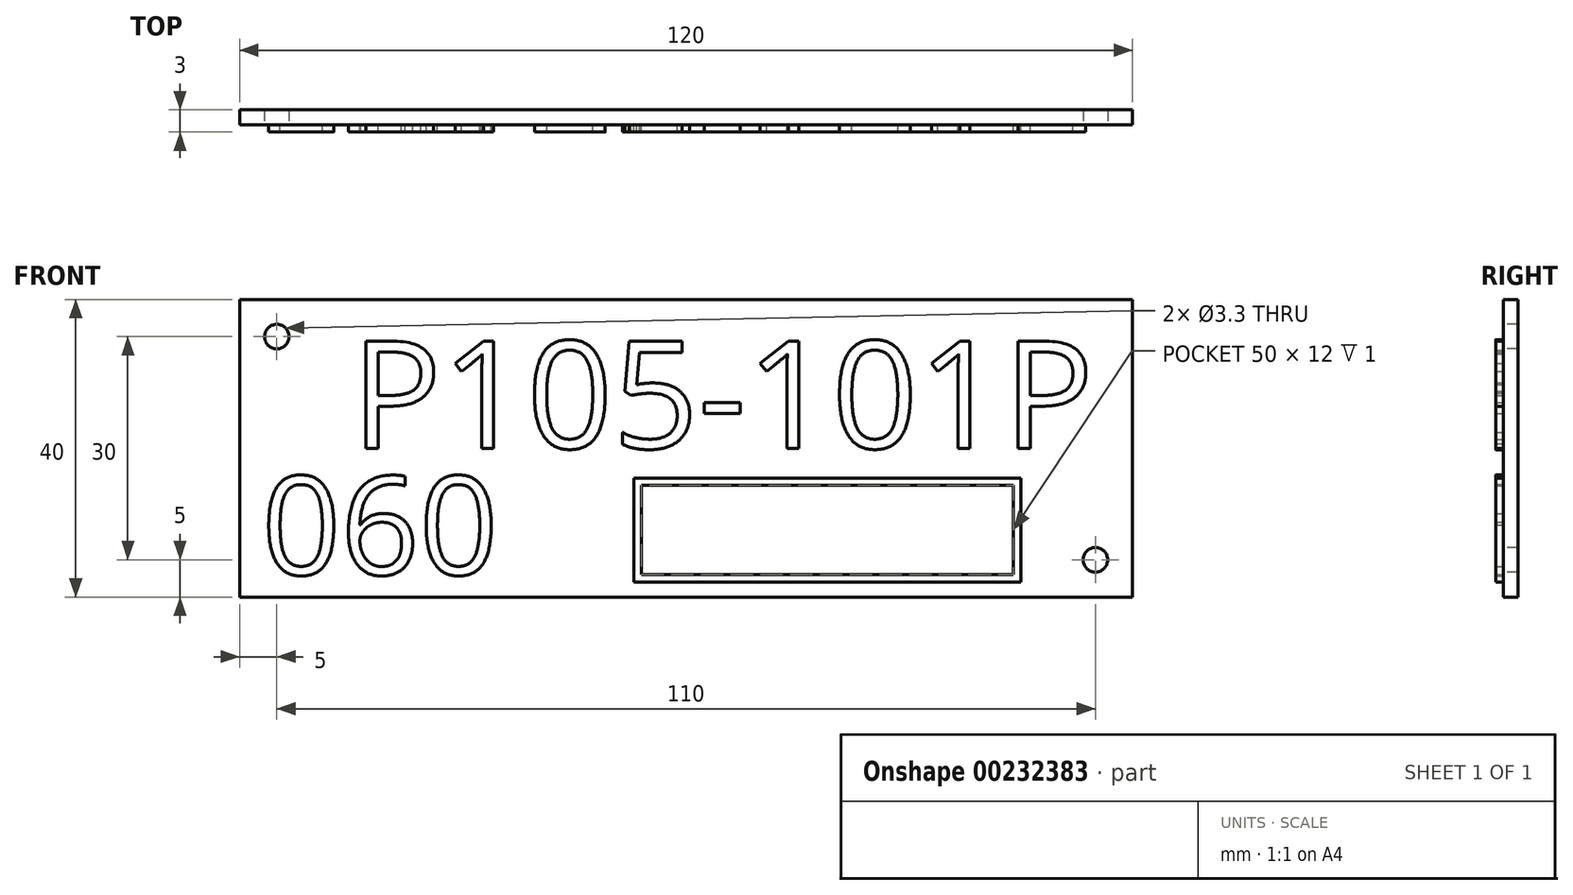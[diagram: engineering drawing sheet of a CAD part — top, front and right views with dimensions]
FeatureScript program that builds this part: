
annotation { "Feature Type Name" : "Feature", "Feature Type Description" : "" }
export const myFeature = defineFeature(function(context is Context, id is Id, definition is map)
    precondition{}
    {
        {
            var Q0;
            Q0=qCreatedBy(makeId("Front.planeOp"),FACE);
            var sketch = newSketch(context, id + "F0", { "sketchPlane" : qUnion([Q0])});
            skLineSegment(sketch, "E0.bottom", {"start": v(60, -20) * mm, "end": v(-60, -20) * mm});
            skLineSegment(sketch, "E0.top", {"start": v(60, 20) * mm, "end": v(-60, 20) * mm});
            skLineSegment(sketch, "E0.left", {"start": v(60, -20) * mm, "end": v(60, 20) * mm});
            skLineSegment(sketch, "E0.right", {"start": v(-60, -20) * mm, "end": v(-60, 20) * mm});
            skPoint(sketch, "E0.middle", {"position": v(0, 0) * mm});
            skSolve(sketch);
        }
        {
            var Q0;
            Q0=makeQuery(id+"F0.imprint","IMPRINT",FACE,{"disambiguationData":[TD([[makeQuery(id+"F0.imprint","IMPRINT",EDGE,{"derivedFrom":sQuery(id+"F0.wireOp",EDGE,"E0.bottom")}),-1.0]])]});
            extrude(context, id + "F1", {"entities" : qUnion([Q0]), "depth" : 2 * mm});
        }
        {
            var Q0;
            Q0=makeQuery(id+"F1.opExtrude","CAP_FACE",FACE,{"disambiguationData":[OSD([sQuery(id+"F0.wireOp",EDGE,"E0.bottom"),sQuery(id+"F0.wireOp",EDGE,"E0.top"),sQuery(id+"F0.wireOp",EDGE,"E0.left"),sQuery(id+"F0.wireOp",EDGE,"E0.right")])],"isStart":false});
            var sketch = newSketch(context, id + "F2", { "sketchPlane" : qUnion([Q0])});
            skPoint(sketch, "E1", {"position": v(-55, 15) * mm});
            skPoint(sketch, "E2", {"position": v(55, -15) * mm});
            skSolve(sketch);
        }
        {
            var Q0;
            Q0=sQuery(id+"F2.wireOp",VERTEX,"E1");
            var Q1;
            Q1=sQuery(id+"F2.wireOp",VERTEX,"E2");
            var Q2;
            Q2=makeQuery(id+"F1.opExtrude","SWEPT_BODY",BODY,{"disambiguationData":[OSD([sQuery(id+"F0.wireOp",EDGE,"E0.bottom"),sQuery(id+"F0.wireOp",EDGE,"E0.top"),sQuery(id+"F0.wireOp",EDGE,"E0.left"),sQuery(id+"F0.wireOp",EDGE,"E0.right")])]});
            hole(context, id + "F3", {"style" : HoleStyle.SIMPLE, "endStyle" : HoleEndStyle.THROUGH, "holeDiameter" : 3.3 * mm, "locations" : qUnion([Q0, Q1]), "scope" : qUnion([Q2]), "isTappedThrough" : true});
        }
        {
            var Q0;
            Q0=makeQuery(id+"F1.opExtrude","CAP_FACE",FACE,{"disambiguationData":[OSD([sQuery(id+"F0.wireOp",EDGE,"E0.bottom"),sQuery(id+"F0.wireOp",EDGE,"E0.top"),sQuery(id+"F0.wireOp",EDGE,"E0.left"),sQuery(id+"F0.wireOp",EDGE,"E0.right")])],"isStart":false});
            var sketch = newSketch(context, id + "F4", { "sketchPlane" : qUnion([Q0])});
            skText(sketch, "E3", { "text": "P105-101P", "fontName": "OpenSans-Regular.ttf"});
            const initialGuessF4  = {"E3": [-0.045, 0, 1, 0, 0.01449]};
            skSetInitialGuess(sketch, initialGuessF4);
            skSolve(sketch);
        }
        {
            var Q0;
            Q0=qSketchRegion(id+"F4",true);
            extrude(context, id + "F5", {"entities" : qUnion([Q0]), "operationType" : NewBodyOperationType.ADD, "depth" : 1 * mm});
        }
        {
            var Q0;
            {var subQ0=sQuery(id+"F0.wireOp",EDGE,"E0.top");var subQ1=sQuery(id+"F0.wireOp",EDGE,"E0.left");var subQ2=sQuery(id+"F0.wireOp",EDGE,"E0.right");var subQ3=sQuery(id+"F0.wireOp",EDGE,"E0.bottom");Q0=makeQuery(id+"F5.boolean.opBoolean","SPLIT",FACE,{"disambiguationData":[TD([makeQuery(id+"F1.opExtrude","SWEPT_FACE",FACE,{"disambiguationData":[OSD([subQ3])]})])],"derivedFrom":makeQuery(id+"F1.opExtrude","CAP_FACE",FACE,{"disambiguationData":[OSD([subQ3,subQ0,subQ1,subQ2])],"isStart":false})});}
            var sketch = newSketch(context, id + "F6", { "sketchPlane" : qUnion([Q0])});
            skText(sketch, "E4", { "text": "060\n", "fontName": "OpenSans-Regular.ttf"});
            const initialGuessF6  = {"E4": [-0.057, -0.017, 1, 0, 0.01332]};
            skSetInitialGuess(sketch, initialGuessF6);
            skSolve(sketch);
        }
        {
            var Q0;
            Q0=qSketchRegion(id+"F6",true);
            extrude(context, id + "F7", {"entities" : qUnion([Q0]), "operationType" : NewBodyOperationType.ADD, "depth" : 1 * mm});
        }
        {
            var Q0;
            {var subQ46=sQuery(id+"F0.wireOp",EDGE,"E0.top");var subQ48=sQuery(id+"F0.wireOp",EDGE,"E0.left");var subQ66=sQuery(id+"F0.wireOp",EDGE,"E0.right");var subQ76=sQuery(id+"F0.wireOp",EDGE,"E0.bottom");var subQ77=makeQuery(id+"F1.opExtrude","SWEPT_FACE",FACE,{"disambiguationData":[OSD([subQ76])]});Q0=makeQuery(id+"F7.boolean.opBoolean","SPLIT",FACE,{"disambiguationData":[TD([subQ77])],"derivedFrom":makeQuery(id+"F5.boolean.opBoolean","SPLIT",FACE,{"disambiguationData":[TD([subQ77])],"derivedFrom":makeQuery(id+"F1.opExtrude","CAP_FACE",FACE,{"disambiguationData":[OSD([subQ76,subQ46,subQ48,subQ66])],"isStart":false})})});}
            var sketch = newSketch(context, id + "F8", { "sketchPlane" : qUnion([Q0])});
            skLineSegment(sketch, "E5.bottom", {"start": v(45, -18) * mm, "end": v(-7, -18) * mm});
            skLineSegment(sketch, "E5.top", {"start": v(45, -4) * mm, "end": v(-7, -4) * mm});
            skLineSegment(sketch, "E5.left", {"start": v(45, -18) * mm, "end": v(45, -4) * mm});
            skLineSegment(sketch, "E5.right", {"start": v(-7, -18) * mm, "end": v(-7, -4) * mm});
            skPoint(sketch, "E5.middle", {"position": v(19, -11) * mm});
            skLineSegment(sketch, "E6.0", {"start": v(44, -5) * mm, "end": v(-6, -5) * mm});
            skLineSegment(sketch, "E6.1", {"start": v(44, -17) * mm, "end": v(44, -5) * mm});
            skLineSegment(sketch, "E6.2", {"start": v(44, -17) * mm, "end": v(-6, -17) * mm});
            skLineSegment(sketch, "E6.3", {"start": v(-6, -17) * mm, "end": v(-6, -5) * mm});
            skSolve(sketch);
        }
        {
            var Q0;
            Q0=makeQuery(id+"F8.imprint","IMPRINT",FACE,{"disambiguationData":[TD([[makeQuery(id+"F8.imprint","IMPRINT",EDGE,{"derivedFrom":sQuery(id+"F8.wireOp",EDGE,"E5.bottom")}),-1.0]])]});
            extrude(context, id + "F9", {"entities" : qUnion([Q0]), "operationType" : NewBodyOperationType.ADD, "depth" : 1 * mm});
        }
    });
